# Revit family: SWC_Chartham WH WC CHWC101 Rev01
name_source: partatom
category: Generic Models
revit_build: Autodesk Revit 2015 (Build: 20140606_1530(x64)
units: mm (PartAtom-declared; Revit-internal decimal feet)

## types (1)
- SWC_WC_CHWC101
    Brand = SanCeram
    Help = http://www.theswc.co.uk
    Manufacturer URL = www.theswc.co.uk
    Mounting brackets = Support brackets & fixings - TSWC117 (supplied seperatly)
    NBS Reference Code = N13 - 300
    NBS Reference Description = WCS AND CISTERNS
    Name = Chartham wall hung WC
    Nominal Length = 520 mm
    Nominal Width = 370 mm
    Pan Mounting = Wall Mounted
    Primary Finishes = Alpine White
    Primary Material = Vitreous China
    Product Family = Sanitary
    Product Group = Wall Hung WC
    Product Information = http://www.theswc.co.uk
    Product SKU = CHWC101
    Rim Type = Boxed Rim
    Seat = Seat & cover white - CHWC109 / Soft close seat & cover white - CHWC110 (Supplied seperatly)
    Seat Colour = White
    Secondary Material = Polished Chrome
    Spare Parts = http://www.theswc.co.uk
    Trap Type = P Trap
    Trapway Tap = Concealed
    Weight = 19 kg

## geometry (parser evidence)
native form markers: Blend x4, Sweep x13
no freeform markers — native parametric forms only
